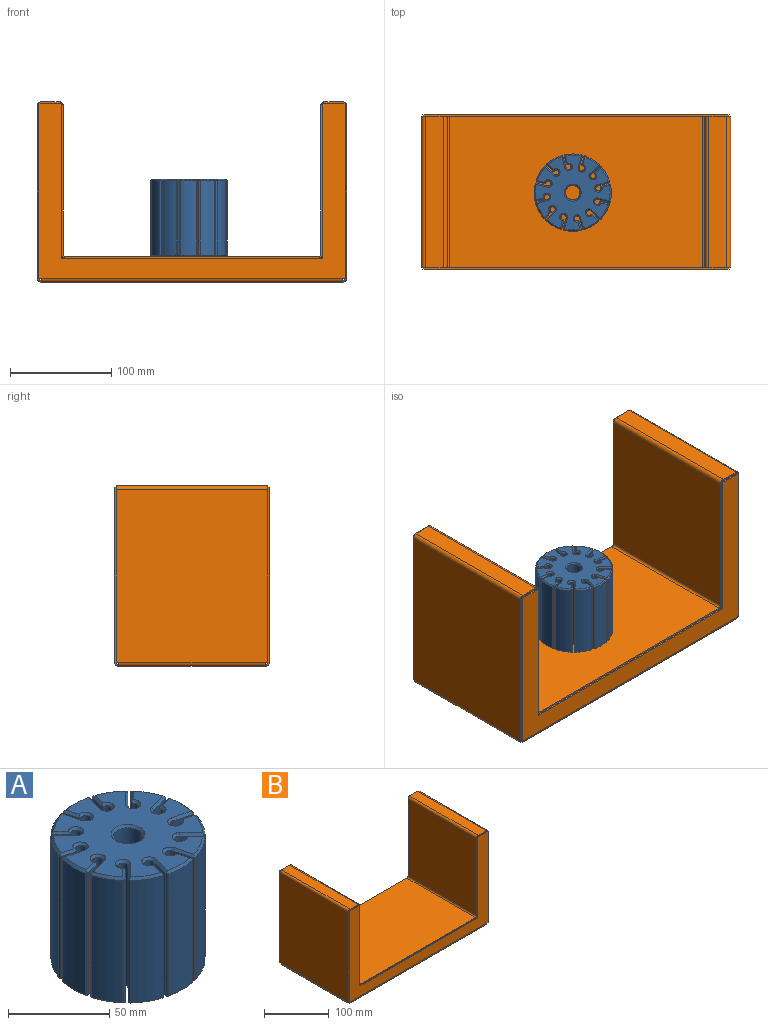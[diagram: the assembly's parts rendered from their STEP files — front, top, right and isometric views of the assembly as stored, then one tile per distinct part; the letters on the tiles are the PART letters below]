
ASSEMBLY  parts=2 mates=1
PART A: 184 faces, bbox 76.2x76.2x76.2 mm
  f0: cylinder r=2.54mm len=73.66mm, axis (0,0,-1), area 881.7mm2, adj f1,f87,f133,f172
  f1: plane 73.66x7.96mm, normal (0.71,-0.71,0), area 828.4mm2, adj f0,f85,f99,f170
  f2: cylinder r=38.1mm len=73.66mm, axis (0,0,-1), area 1179mm2, adj f83,f99,f100,f168
  f3: plane 73.66x7.12mm, normal (-0.97,0.26,0), area 543mm2, adj f81,f100,f101,f166
  f4: cylinder r=2.54mm len=73.66mm, axis (0,0,-1), area 881.7mm2, adj f5,f79,f101,f164
  f5: plane 73.66x10.87mm, normal (0.97,-0.26,0), area 828.4mm2, adj f4,f77,f102,f162
  f6: cylinder r=38.1mm len=73.66mm, axis (0,0,-1), area 1179mm2, adj f75,f102,f103,f160
  f7: plane 73.66x7.12mm, normal (-0.97,-0.26,0), area 543mm2, adj f73,f103,f104,f158
  f8: cylinder r=2.54mm len=73.66mm, axis (0,0,-1), area 881.7mm2, adj f9,f71,f104,f156
  f9: plane 73.66x10.86mm, normal (0.97,0.26,0), area 828.4mm2, adj f8,f69,f105,f154
  f10: cylinder r=38.1mm len=73.66mm, axis (0,0,-1), area 1179mm2, adj f67,f105,f106,f152
  f11: plane 73.66x5.22mm, normal (-0.71,-0.71,0), area 543mm2, adj f65,f106,f107,f150
  f12: cylinder r=2.54mm len=73.66mm, axis (0,0,-1), area 881.7mm2, adj f13,f63,f107,f148
  f13: plane 73.66x8.88mm, normal (0.71,0.71,0), area 923.6mm2, adj f12,f14,f61,f146
  f14: cylinder r=38.1mm len=73.66mm, axis (0,0,-1), area 1275.7mm2, adj f13,f59,f108,f144
  f15: plane 73.66x7.12mm, normal (-0.26,-0.97,0), area 543mm2, adj f57,f108,f109,f142
  f16: cylinder r=2.54mm len=73.66mm, axis (0,0,-1), area 881.7mm2, adj f17,f55,f109,f140
  f17: plane 73.66x10.87mm, normal (0.26,0.97,0), area 828.4mm2, adj f16,f53,f110,f138
  f18: cylinder r=38.1mm len=73.66mm, axis (0,0,-1), area 1179mm2, adj f51,f110,f111,f136
  f19: plane 73.66x7.12mm, normal (0.26,-0.97,0), area 543mm2, adj f50,f111,f112,f135
  f20: cylinder r=2.54mm len=73.66mm, axis (0,0,-1), area 881.7mm2, adj f21,f52,f112,f137
  f21: plane 73.66x10.86mm, normal (-0.26,0.97,0), area 828.4mm2, adj f20,f54,f113,f139
  f22: cylinder r=38.1mm len=73.66mm, axis (0,0,-1), area 1179mm2, adj f56,f113,f114,f141
  f23: plane 73.66x5.22mm, normal (0.71,-0.71,0), area 543mm2, adj f58,f114,f115,f143
  f24: cylinder r=2.54mm len=73.66mm, axis (0,0,-1), area 881.7mm2, adj f25,f60,f115,f145
  f25: plane 73.66x7.96mm, normal (-0.71,0.71,0), area 828.4mm2, adj f24,f62,f116,f147
  f26: cylinder r=38.1mm len=73.66mm, axis (0,0,-1), area 1179mm2, adj f64,f116,f117,f149
  f27: plane 73.66x7.12mm, normal (0.97,-0.26,0), area 543mm2, adj f66,f117,f118,f151
  f28: cylinder r=2.54mm len=73.66mm, axis (0,0,-1), area 881.7mm2, adj f29,f68,f118,f153
  f29: plane 73.66x10.87mm, normal (-0.97,0.26,0), area 828.4mm2, adj f28,f70,f119,f155
  f30: cylinder r=38.1mm len=73.66mm, axis (0,0,-1), area 1179mm2, adj f72,f119,f120,f157
  f31: plane 73.66x7.12mm, normal (0.97,0.26,0), area 543mm2, adj f74,f120,f121,f159
  f32: cylinder r=2.54mm len=73.66mm, axis (0,0,-1), area 881.7mm2, adj f33,f76,f121,f161
  f33: plane 73.66x10.86mm, normal (-0.97,-0.26,0), area 828.4mm2, adj f32,f78,f122,f163
  f34: cylinder r=38.1mm len=73.66mm, axis (0,0,-1), area 1179mm2, adj f80,f122,f123,f165
  f35: plane 73.66x5.22mm, normal (0.71,0.71,0), area 543mm2, adj f82,f123,f124,f167
  f36: cylinder r=2.54mm len=73.66mm, axis (0,0,-1), area 881.7mm2, adj f37,f84,f124,f169
  f37: plane 73.66x7.96mm, normal (-0.71,-0.71,0), area 828.4mm2, adj f36,f86,f125,f171
  f38: cylinder r=38.1mm len=73.66mm, axis (0,0,-1), area 1179mm2, adj f88,f125,f126,f173
  f39: plane 73.66x7.12mm, normal (0.26,0.97,0), area 543mm2, adj f90,f126,f127,f175
  f40: cylinder r=2.54mm len=73.66mm, axis (0,0,-1), area 881.7mm2, adj f41,f92,f127,f177
  f41: plane 73.66x10.87mm, normal (-0.26,-0.97,0), area 828.4mm2, adj f40,f94,f128,f179
  f42: cylinder r=38.1mm len=73.66mm, axis (0,0,-1), area 1179mm2, adj f96,f128,f129,f181
  f43: plane 73.66x7.12mm, normal (-0.26,0.97,0), area 543mm2, adj f97,f129,f130,f182
  f44: cylinder r=2.54mm len=73.66mm, axis (0,0,-1), area 881.7mm2, adj f45,f95,f130,f180
  f45: plane 73.66x10.86mm, normal (0.26,-0.97,0), area 828.4mm2, adj f44,f93,f131,f178
  f46: cylinder r=38.1mm len=73.66mm, axis (0,0,-1), area 1179mm2, adj f91,f131,f132,f176
  f47: plane 73.66x5.22mm, normal (-0.71,0.71,0), area 543mm2, adj f89,f132,f133,f174
  f48: plane 73.66x73.66mm, normal (0,0,-1), area 3114.7mm2, adj f50,f51,f52,f53,f54,f55,f56,f57
  f49: cylinder r=7.14mm len=73.66mm, axis (0,0,-1), area 3303.3mm2, adj f98,f183
  f50: plane 8.93x3.2mm, normal (0.18,-0.68,-0.71), area 15.1mm2, adj f19,f48,f51,f52,f111,f112
  f51: cone r=38.1mm half-angle=45deg, axis (0,0,1), area 30.1mm2, adj f18,f48,f50,f53,f110,f111
  f52: cone r=3.81mm half-angle=45deg, axis (0,0,-1), area 27.7mm2, adj f20,f48,f50,f54,f112
  f53: plane 11.85x4.18mm, normal (0.18,0.68,-0.71), area 21.1mm2, adj f17,f48,f51,f55,f110
  f54: plane 11.98x4.16mm, normal (-0.18,0.68,-0.71), area 21.1mm2, adj f21,f48,f52,f56,f113
  f55: cone r=3.81mm half-angle=45deg, axis (0,0,-1), area 27.7mm2, adj f16,f48,f53,f57,f109
  f56: cone r=38.1mm half-angle=45deg, axis (0,0,1), area 30.1mm2, adj f22,f48,f54,f58,f113,f114
  f57: plane 8.96x3.18mm, normal (-0.18,-0.68,-0.71), area 15.1mm2, adj f15,f48,f55,f59,f108,f109
  f58: plane 6.58x6.52mm, normal (0.5,-0.5,-0.71), area 15.1mm2, adj f23,f48,f56,f60,f114,f115
  f59: cone r=38.1mm half-angle=45deg, axis (0,0,1), area 30.4mm2, adj f14,f48,f57,f61,f108
  f60: cone r=3.81mm half-angle=45deg, axis (0,0,-1), area 27.7mm2, adj f24,f48,f58,f62,f115
  f61: plane 9.77x8.9mm, normal (0.5,0.5,-0.71), area 21.4mm2, adj f13,f48,f59,f63
  f62: plane 9.22x8.88mm, normal (-0.5,0.5,-0.71), area 21.1mm2, adj f25,f48,f60,f64,f116
  f63: cone r=3.81mm half-angle=45deg, axis (0,0,-1), area 27.7mm2, adj f12,f48,f61,f65,f107
  f64: cone r=38.1mm half-angle=45deg, axis (0,0,1), area 30.1mm2, adj f26,f48,f62,f66,f116,f117
  f65: plane 6.58x6.52mm, normal (-0.5,-0.5,-0.71), area 15.1mm2, adj f11,f48,f63,f67,f106,f107
  f66: plane 8.96x3.18mm, normal (0.68,-0.18,-0.71), area 15.1mm2, adj f27,f48,f64,f68,f117,f118
  f67: cone r=38.1mm half-angle=45deg, axis (0,0,1), area 30.1mm2, adj f10,f48,f65,f69,f105,f106
  f68: cone r=3.81mm half-angle=45deg, axis (0,0,-1), area 27.7mm2, adj f28,f48,f66,f70,f118
  f69: plane 11.98x4.16mm, normal (0.68,0.18,-0.71), area 21.1mm2, adj f9,f48,f67,f71,f105
  f70: plane 11.85x4.18mm, normal (-0.68,0.18,-0.71), area 21.1mm2, adj f29,f48,f68,f72,f119
  f71: cone r=3.81mm half-angle=45deg, axis (0,0,-1), area 27.7mm2, adj f8,f48,f69,f73,f104
  f72: cone r=38.1mm half-angle=45deg, axis (0,0,1), area 30.1mm2, adj f30,f48,f70,f74,f119,f120
  f73: plane 8.93x3.2mm, normal (-0.68,-0.18,-0.71), area 15.1mm2, adj f7,f48,f71,f75,f103,f104
  f74: plane 8.93x3.2mm, normal (0.68,0.18,-0.71), area 15.1mm2, adj f31,f48,f72,f76,f120,f121
  f75: cone r=38.1mm half-angle=45deg, axis (0,0,1), area 30.1mm2, adj f6,f48,f73,f77,f102,f103
  f76: cone r=3.81mm half-angle=45deg, axis (0,0,-1), area 27.7mm2, adj f32,f48,f74,f78,f121
  f77: plane 11.85x4.18mm, normal (0.68,-0.18,-0.71), area 21.1mm2, adj f5,f48,f75,f79,f102
  f78: plane 11.98x4.16mm, normal (-0.68,-0.18,-0.71), area 21.1mm2, adj f33,f48,f76,f80,f122
  f79: cone r=3.81mm half-angle=45deg, axis (0,0,-1), area 27.7mm2, adj f4,f48,f77,f81,f101
  f80: cone r=38.1mm half-angle=45deg, axis (0,0,1), area 30.1mm2, adj f34,f48,f78,f82,f122,f123
  f81: plane 8.96x3.18mm, normal (-0.68,0.18,-0.71), area 15.1mm2, adj f3,f48,f79,f83,f100,f101
  f82: plane 6.58x6.52mm, normal (0.5,0.5,-0.71), area 15.1mm2, adj f35,f48,f80,f84,f123,f124
  f83: cone r=38.1mm half-angle=45deg, axis (0,0,1), area 30.1mm2, adj f2,f48,f81,f85,f99,f100
  f84: cone r=3.81mm half-angle=45deg, axis (0,0,-1), area 27.7mm2, adj f36,f48,f82,f86,f124
  f85: plane 9.22x8.88mm, normal (0.5,-0.5,-0.71), area 21.1mm2, adj f1,f48,f83,f87,f99
  f86: plane 9.22x8.88mm, normal (-0.5,-0.5,-0.71), area 21.1mm2, adj f37,f48,f84,f88,f125
  f87: cone r=3.81mm half-angle=45deg, axis (0,0,-1), area 27.7mm2, adj f0,f48,f85,f89,f133
  f88: cone r=38.1mm half-angle=45deg, axis (0,0,1), area 30.1mm2, adj f38,f48,f86,f90,f125,f126
  f89: plane 6.58x6.52mm, normal (-0.5,0.5,-0.71), area 15.1mm2, adj f47,f48,f87,f91,f132,f133
  f90: plane 8.96x3.18mm, normal (0.18,0.68,-0.71), area 15.1mm2, adj f39,f48,f88,f92,f126,f127
  f91: cone r=38.1mm half-angle=45deg, axis (0,0,1), area 30.1mm2, adj f46,f48,f89,f93,f131,f132
  f92: cone r=3.81mm half-angle=45deg, axis (0,0,-1), area 27.7mm2, adj f40,f48,f90,f94,f127
  f93: plane 11.98x4.16mm, normal (0.18,-0.68,-0.71), area 21.1mm2, adj f45,f48,f91,f95,f131
  f94: plane 11.85x4.18mm, normal (-0.18,-0.68,-0.71), area 21.1mm2, adj f41,f48,f92,f96,f128
  f95: cone r=3.81mm half-angle=45deg, axis (0,0,-1), area 27.7mm2, adj f44,f48,f93,f97,f130
  f96: cone r=38.1mm half-angle=45deg, axis (0,0,1), area 30.1mm2, adj f42,f48,f94,f97,f128,f129
  f97: plane 8.93x3.2mm, normal (-0.18,0.68,-0.71), area 15.1mm2, adj f43,f48,f95,f96,f129,f130
  f98: cone r=7.14mm half-angle=45deg, axis (0,0,-1), area 87.7mm2, adj f48,f49
  f99: cylinder r=1.27mm len=74.42mm, axis (0,0,-1), area 150.7mm2, adj f1,f2,f83,f85,f168,f170
  f100: cylinder r=1.27mm len=74.46mm, axis (0,0,-1), area 154mm2, adj f2,f3,f81,f83,f166,f168
  f101: cylinder r=1.27mm len=74.53mm, axis (0,0,-1), area 147.5mm2, adj f3,f4,f79,f81,f164,f166
  f102: cylinder r=1.27mm len=74.42mm, axis (0,0,-1), area 150.7mm2, adj f5,f6,f75,f77,f160,f162
  f103: cylinder r=1.27mm len=74.46mm, axis (0,0,-1), area 154mm2, adj f6,f7,f73,f75,f158,f160
  f104: cylinder r=1.27mm len=74.53mm, axis (0,0,-1), area 147.5mm2, adj f7,f8,f71,f73,f156,f158
  f105: cylinder r=1.27mm len=74.42mm, axis (0,0,-1), area 150.7mm2, adj f9,f10,f67,f69,f152,f154
  f106: cylinder r=1.27mm len=74.46mm, axis (0,0,-1), area 154mm2, adj f10,f11,f65,f67,f150,f152
  f107: cylinder r=1.27mm len=74.53mm, axis (0,0,-1), area 147.5mm2, adj f11,f12,f63,f65,f148,f150
  f108: cylinder r=1.27mm len=74.46mm, axis (0,0,-1), area 154mm2, adj f14,f15,f57,f59,f142,f144
  f109: cylinder r=1.27mm len=74.53mm, axis (0,0,-1), area 147.5mm2, adj f15,f16,f55,f57,f140,f142
  f110: cylinder r=1.27mm len=74.42mm, axis (0,0,-1), area 150.7mm2, adj f17,f18,f51,f53,f136,f138
  f111: cylinder r=1.27mm len=74.46mm, axis (0,0,-1), area 154mm2, adj f18,f19,f50,f51,f135,f136
  f112: cylinder r=1.27mm len=74.53mm, axis (0,0,-1), area 147.5mm2, adj f19,f20,f50,f52,f135,f137
  f113: cylinder r=1.27mm len=74.42mm, axis (0,0,-1), area 150.7mm2, adj f21,f22,f54,f56,f139,f141
  f114: cylinder r=1.27mm len=74.46mm, axis (0,0,-1), area 154mm2, adj f22,f23,f56,f58,f141,f143
  f115: cylinder r=1.27mm len=74.53mm, axis (0,0,-1), area 147.5mm2, adj f23,f24,f58,f60,f143,f145
  f116: cylinder r=1.27mm len=74.42mm, axis (0,0,-1), area 150.7mm2, adj f25,f26,f62,f64,f147,f149
  f117: cylinder r=1.27mm len=74.46mm, axis (0,0,-1), area 154mm2, adj f26,f27,f64,f66,f149,f151
  f118: cylinder r=1.27mm len=74.53mm, axis (0,0,-1), area 147.5mm2, adj f27,f28,f66,f68,f151,f153
  f119: cylinder r=1.27mm len=74.42mm, axis (0,0,-1), area 150.7mm2, adj f29,f30,f70,f72,f155,f157
  f120: cylinder r=1.27mm len=74.46mm, axis (0,0,-1), area 154mm2, adj f30,f31,f72,f74,f157,f159
  f121: cylinder r=1.27mm len=74.53mm, axis (0,0,-1), area 147.5mm2, adj f31,f32,f74,f76,f159,f161
  f122: cylinder r=1.27mm len=74.42mm, axis (0,0,-1), area 150.7mm2, adj f33,f34,f78,f80,f163,f165
  f123: cylinder r=1.27mm len=74.46mm, axis (0,0,-1), area 154mm2, adj f34,f35,f80,f82,f165,f167
  f124: cylinder r=1.27mm len=74.53mm, axis (0,0,-1), area 147.5mm2, adj f35,f36,f82,f84,f167,f169
  f125: cylinder r=1.27mm len=74.42mm, axis (0,0,-1), area 150.7mm2, adj f37,f38,f86,f88,f171,f173
  f126: cylinder r=1.27mm len=74.46mm, axis (0,0,-1), area 154mm2, adj f38,f39,f88,f90,f173,f175
  f127: cylinder r=1.27mm len=74.53mm, axis (0,0,-1), area 147.5mm2, adj f39,f40,f90,f92,f175,f177
  f128: cylinder r=1.27mm len=74.42mm, axis (0,0,-1), area 150.7mm2, adj f41,f42,f94,f96,f179,f181
  f129: cylinder r=1.27mm len=74.46mm, axis (0,0,-1), area 154mm2, adj f42,f43,f96,f97,f181,f182
  f130: cylinder r=1.27mm len=74.53mm, axis (0,0,-1), area 147.5mm2, adj f43,f44,f95,f97,f180,f182
  f131: cylinder r=1.27mm len=74.42mm, axis (0,0,-1), area 150.7mm2, adj f45,f46,f91,f93,f176,f178
  f132: cylinder r=1.27mm len=74.46mm, axis (0,0,-1), area 154mm2, adj f46,f47,f89,f91,f174,f176
  f133: cylinder r=1.27mm len=74.53mm, axis (0,0,-1), area 147.5mm2, adj f0,f47,f87,f89,f172,f174
  f134: plane 73.66x73.66mm, normal (0,0,1), area 3114.7mm2, adj f135,f136,f137,f138,f139,f140,f141,f142
  f135: plane 8.93x3.2mm, normal (0.18,-0.68,0.71), area 15.1mm2, adj f19,f111,f112,f134,f136,f137
  f136: cone r=38.1mm half-angle=45deg, axis (0,0,-1), area 30.1mm2, adj f18,f110,f111,f134,f135,f138
  f137: cone r=3.81mm half-angle=45deg, axis (0,0,1), area 27.7mm2, adj f20,f112,f134,f135,f139
  f138: plane 11.85x4.18mm, normal (0.18,0.68,0.71), area 21.1mm2, adj f17,f110,f134,f136,f140
  f139: plane 11.98x4.16mm, normal (-0.18,0.68,0.71), area 21.1mm2, adj f21,f113,f134,f137,f141
  f140: cone r=3.81mm half-angle=45deg, axis (0,0,1), area 27.7mm2, adj f16,f109,f134,f138,f142
  f141: cone r=38.1mm half-angle=45deg, axis (0,0,-1), area 30.1mm2, adj f22,f113,f114,f134,f139,f143
  f142: plane 8.96x3.18mm, normal (-0.18,-0.68,0.71), area 15.1mm2, adj f15,f108,f109,f134,f140,f144
  f143: plane 6.58x6.52mm, normal (0.5,-0.5,0.71), area 15.1mm2, adj f23,f114,f115,f134,f141,f145
  f144: cone r=38.1mm half-angle=45deg, axis (0,0,-1), area 30.4mm2, adj f14,f108,f134,f142,f146
  f145: cone r=3.81mm half-angle=45deg, axis (0,0,1), area 27.7mm2, adj f24,f115,f134,f143,f147
  f146: plane 9.77x8.9mm, normal (0.5,0.5,0.71), area 21.4mm2, adj f13,f134,f144,f148
  f147: plane 9.22x8.88mm, normal (-0.5,0.5,0.71), area 21.1mm2, adj f25,f116,f134,f145,f149
  f148: cone r=3.81mm half-angle=45deg, axis (0,0,1), area 27.7mm2, adj f12,f107,f134,f146,f150
  f149: cone r=38.1mm half-angle=45deg, axis (0,0,-1), area 30.1mm2, adj f26,f116,f117,f134,f147,f151
  f150: plane 6.58x6.52mm, normal (-0.5,-0.5,0.71), area 15.1mm2, adj f11,f106,f107,f134,f148,f152
  f151: plane 8.96x3.18mm, normal (0.68,-0.18,0.71), area 15.1mm2, adj f27,f117,f118,f134,f149,f153
  f152: cone r=38.1mm half-angle=45deg, axis (0,0,-1), area 30.1mm2, adj f10,f105,f106,f134,f150,f154
  f153: cone r=3.81mm half-angle=45deg, axis (0,0,1), area 27.7mm2, adj f28,f118,f134,f151,f155
  f154: plane 11.98x4.16mm, normal (0.68,0.18,0.71), area 21.1mm2, adj f9,f105,f134,f152,f156
  f155: plane 11.85x4.18mm, normal (-0.68,0.18,0.71), area 21.1mm2, adj f29,f119,f134,f153,f157
  f156: cone r=3.81mm half-angle=45deg, axis (0,0,1), area 27.7mm2, adj f8,f104,f134,f154,f158
  f157: cone r=38.1mm half-angle=45deg, axis (0,0,-1), area 30.1mm2, adj f30,f119,f120,f134,f155,f159
  f158: plane 8.93x3.2mm, normal (-0.68,-0.18,0.71), area 15.1mm2, adj f7,f103,f104,f134,f156,f160
  f159: plane 8.93x3.2mm, normal (0.68,0.18,0.71), area 15.1mm2, adj f31,f120,f121,f134,f157,f161
  f160: cone r=38.1mm half-angle=45deg, axis (0,0,-1), area 30.1mm2, adj f6,f102,f103,f134,f158,f162
  f161: cone r=3.81mm half-angle=45deg, axis (0,0,1), area 27.7mm2, adj f32,f121,f134,f159,f163
  f162: plane 11.85x4.18mm, normal (0.68,-0.18,0.71), area 21.1mm2, adj f5,f102,f134,f160,f164
  f163: plane 11.98x4.16mm, normal (-0.68,-0.18,0.71), area 21.1mm2, adj f33,f122,f134,f161,f165
  f164: cone r=3.81mm half-angle=45deg, axis (0,0,1), area 27.7mm2, adj f4,f101,f134,f162,f166
  f165: cone r=38.1mm half-angle=45deg, axis (0,0,-1), area 30.1mm2, adj f34,f122,f123,f134,f163,f167
  f166: plane 8.96x3.18mm, normal (-0.68,0.18,0.71), area 15.1mm2, adj f3,f100,f101,f134,f164,f168
  f167: plane 6.58x6.52mm, normal (0.5,0.5,0.71), area 15.1mm2, adj f35,f123,f124,f134,f165,f169
  f168: cone r=38.1mm half-angle=45deg, axis (0,0,-1), area 30.1mm2, adj f2,f99,f100,f134,f166,f170
  f169: cone r=3.81mm half-angle=45deg, axis (0,0,1), area 27.7mm2, adj f36,f124,f134,f167,f171
  f170: plane 9.22x8.88mm, normal (0.5,-0.5,0.71), area 21.1mm2, adj f1,f99,f134,f168,f172
  f171: plane 9.22x8.88mm, normal (-0.5,-0.5,0.71), area 21.1mm2, adj f37,f125,f134,f169,f173
  f172: cone r=3.81mm half-angle=45deg, axis (0,0,1), area 27.7mm2, adj f0,f133,f134,f170,f174
  f173: cone r=38.1mm half-angle=45deg, axis (0,0,-1), area 30.1mm2, adj f38,f125,f126,f134,f171,f175
  f174: plane 6.58x6.52mm, normal (-0.5,0.5,0.71), area 15.1mm2, adj f47,f132,f133,f134,f172,f176
  f175: plane 8.96x3.18mm, normal (0.18,0.68,0.71), area 15.1mm2, adj f39,f126,f127,f134,f173,f177
  f176: cone r=38.1mm half-angle=45deg, axis (0,0,-1), area 30.1mm2, adj f46,f131,f132,f134,f174,f178
  f177: cone r=3.81mm half-angle=45deg, axis (0,0,1), area 27.7mm2, adj f40,f127,f134,f175,f179
  f178: plane 11.98x4.16mm, normal (0.18,-0.68,0.71), area 21.1mm2, adj f45,f131,f134,f176,f180
  f179: plane 11.85x4.18mm, normal (-0.18,-0.68,0.71), area 21.1mm2, adj f41,f128,f134,f177,f181
  f180: cone r=3.81mm half-angle=45deg, axis (0,0,1), area 27.7mm2, adj f44,f130,f134,f178,f182
  f181: cone r=38.1mm half-angle=45deg, axis (0,0,-1), area 30.1mm2, adj f42,f128,f129,f134,f179,f182
  f182: plane 8.93x3.2mm, normal (-0.18,0.68,0.71), area 15.1mm2, adj f43,f129,f130,f134,f180,f181
  f183: cone r=7.14mm half-angle=45deg, axis (0,0,1), area 87.7mm2, adj f49,f134
PART B: 96 faces, bbox 304.8x152.4x177.8 mm
  f0: plane 2.26x1.59mm, normal (0,0,-1), area 3.6mm2, adj f6,f9,f10,f28
  f1: plane 22.17x1.59mm, normal (0,0,1), area 35.2mm2, adj f2,f8,f9,f10
  f2: plane 152.4x1.59mm, normal (1,0,0), area 241.9mm2, adj f1,f3,f9,f10
  f3: plane 257.23x1.59mm, normal (0,0,1), area 408.3mm2, adj f2,f4,f9,f10
  f4: plane 152.4x1.59mm, normal (-1,0,0), area 241.9mm2, adj f3,f5,f9,f10
  f5: plane 22.17x1.59mm, normal (0,0,1), area 35.2mm2, adj f4,f6,f9,f10
  f6: plane 172.31x1.59mm, normal (1,0,0), area 273.5mm2, adj f0,f5,f9,f10
  f7: plane 2.26x1.59mm, normal (0,0,-1), area 3.6mm2, adj f8,f9,f10,f29
  f8: plane 172.31x1.59mm, normal (-1,0,0), area 273.5mm2, adj f1,f7,f9,f10
  f9: plane 301.57x172.31mm, normal (0,1,0), area 12764.1mm2, adj f0,f1,f2,f3,f4,f5,f6,f7
  f10: plane 301.57x172.31mm, normal (0,-1,0), area 12764.1mm2, adj f0,f1,f2,f3,f4,f5,f6,f7
  f11: plane 2.26x1.59mm, normal (0,0,-1), area 3.6mm2, adj f17,f20,f21,f23
  f12: plane 22.17x1.59mm, normal (0,0,1), area 35.2mm2, adj f13,f19,f20,f21
  f13: plane 152.4x1.59mm, normal (-1,0,0), area 241.9mm2, adj f12,f14,f20,f21
  f14: plane 257.23x1.59mm, normal (0,0,1), area 408.3mm2, adj f13,f15,f20,f21
  f15: plane 152.4x1.59mm, normal (1,0,0), area 241.9mm2, adj f14,f16,f20,f21
  f16: plane 22.17x1.59mm, normal (0,0,1), area 35.2mm2, adj f15,f17,f20,f21
  f17: plane 172.31x1.59mm, normal (-1,0,0), area 273.5mm2, adj f11,f16,f20,f21
  f18: plane 2.26x1.59mm, normal (0,0,-1), area 3.6mm2, adj f19,f20,f21,f22
  f19: plane 172.31x1.59mm, normal (1,0,0), area 273.5mm2, adj f12,f18,f20,f21
  f20: plane 301.57x172.31mm, normal (0,-1,0), area 12764.1mm2, adj f11,f12,f13,f14,f15,f16,f17,f18
  f21: plane 301.57x172.31mm, normal (0,1,0), area 12764.1mm2, adj f11,f12,f13,f14,f15,f16,f17,f18
  f22: plane 3.87x3.87mm, normal (1,0,0), area 7.7mm2, adj f18,f24,f25,f32
  f23: plane 3.87x3.87mm, normal (-1,0,0), area 7.7mm2, adj f11,f24,f25,f42
  f24: cylinder r=3.87mm len=297.05mm, axis (1,0,0), area 1807.4mm2, adj f20,f22,f23,f26
  f25: cylinder r=2.29mm len=297.05mm, axis (1,0,0), area 1066.7mm2, adj f21,f22,f23,f27
  f26: plane 297.05x144.65mm, normal (0,0,-1), area 42969.6mm2, adj f24,f30,f34,f44
  f27: plane 297.05x144.65mm, normal (0,0,1), area 42969.6mm2, adj f25,f31,f35,f45
  f28: plane 3.87x3.87mm, normal (1,0,0), area 7.7mm2, adj f0,f30,f31,f33
  f29: plane 3.87x3.87mm, normal (-1,0,0), area 7.7mm2, adj f7,f30,f31,f43
  f30: cylinder r=3.87mm len=297.05mm, axis (1,0,0), area 1807.4mm2, adj f9,f26,f28,f29
  f31: cylinder r=2.29mm len=297.05mm, axis (1,0,0), area 1066.7mm2, adj f10,f27,f28,f29
  f32: plane 3.87x3.87mm, normal (0,-1,0), area 7.7mm2, adj f22,f34,f35,f36
  f33: plane 3.87x3.87mm, normal (0,1,0), area 7.7mm2, adj f28,f34,f35,f38
  f34: cylinder r=3.87mm len=144.65mm, axis (0,-1,0), area 880.1mm2, adj f26,f32,f33,f40
  f35: cylinder r=2.29mm len=144.65mm, axis (0,-1,0), area 519.4mm2, adj f27,f32,f33,f41
  f36: plane 2.26x1.59mm, normal (0,0,-1), area 3.6mm2, adj f32,f37,f40,f41
  f37: plane 170.05x1.59mm, normal (0,-1,0), area 270mm2, adj f36,f40,f41,f46
  f38: plane 2.26x1.59mm, normal (0,0,-1), area 3.6mm2, adj f33,f39,f40,f41
  f39: plane 170.05x1.59mm, normal (0,1,0), area 270mm2, adj f38,f40,f41,f47
  f40: plane 170.05x149.17mm, normal (1,0,0), area 25367.5mm2, adj f34,f36,f37,f38,f39,f48
  f41: plane 170.05x149.17mm, normal (-1,0,0), area 25367.5mm2, adj f35,f36,f37,f38,f39,f49
  f42: plane 3.87x3.87mm, normal (0,-1,0), area 7.7mm2, adj f23,f44,f45,f52
  f43: plane 3.87x3.87mm, normal (0,1,0), area 7.7mm2, adj f29,f44,f45,f50
  f44: cylinder r=3.87mm len=144.65mm, axis (0,-1,0), area 880.1mm2, adj f26,f42,f43,f54
  f45: cylinder r=2.29mm len=144.65mm, axis (0,-1,0), area 519.4mm2, adj f27,f42,f43,f55
  f46: plane 3.87x3.87mm, normal (0,-1,0), area 7.7mm2, adj f37,f48,f49,f56
  f47: plane 3.87x3.87mm, normal (0,1,0), area 7.7mm2, adj f39,f48,f49,f57
  f48: cylinder r=3.87mm len=149.17mm, axis (0,-1,0), area 907.6mm2, adj f40,f46,f47,f58
  f49: cylinder r=2.29mm len=149.17mm, axis (0,-1,0), area 535.7mm2, adj f41,f46,f47,f59
  f50: plane 2.26x1.59mm, normal (0,0,-1), area 3.6mm2, adj f43,f51,f54,f55
  f51: plane 170.05x1.59mm, normal (0,1,0), area 270mm2, adj f50,f54,f55,f61
  f52: plane 2.26x1.59mm, normal (0,0,-1), area 3.6mm2, adj f42,f53,f54,f55
  f53: plane 170.05x1.59mm, normal (0,-1,0), area 270mm2, adj f52,f54,f55,f60
  f54: plane 170.05x149.17mm, normal (-1,0,0), area 25367.5mm2, adj f44,f50,f51,f52,f53,f62
  f55: plane 170.05x149.17mm, normal (1,0,0), area 25367.5mm2, adj f45,f50,f51,f52,f53,f63
  f56: plane 17.65x1.59mm, normal (0,-1,0), area 28mm2, adj f46,f58,f59,f64
  f57: plane 17.65x1.59mm, normal (0,1,0), area 28mm2, adj f47,f58,f59,f65
  f58: plane 149.17x17.65mm, normal (0,0,1), area 2633.4mm2, adj f48,f56,f57,f66
  f59: plane 149.17x17.65mm, normal (0,0,-1), area 2633.4mm2, adj f49,f56,f57,f67
  f60: plane 3.87x3.87mm, normal (0,-1,0), area 7.7mm2, adj f53,f62,f63,f68
  f61: plane 3.87x3.87mm, normal (0,1,0), area 7.7mm2, adj f51,f62,f63,f69
  f62: cylinder r=3.87mm len=149.17mm, axis (0,-1,0), area 907.6mm2, adj f54,f60,f61,f70
  f63: cylinder r=2.29mm len=149.17mm, axis (0,-1,0), area 535.7mm2, adj f55,f60,f61,f71
  f64: plane 3.87x3.87mm, normal (0,-1,0), area 7.7mm2, adj f56,f66,f67,f77
  f65: plane 3.87x3.87mm, normal (0,1,0), area 7.7mm2, adj f57,f66,f67,f76
  f66: cylinder r=3.87mm len=149.17mm, axis (0,-1,0), area 907.6mm2, adj f58,f64,f65,f78
  f67: cylinder r=2.29mm len=149.17mm, axis (0,-1,0), area 535.7mm2, adj f59,f64,f65,f79
  f68: plane 17.65x1.59mm, normal (0,-1,0), area 28mm2, adj f60,f70,f71,f72
  f69: plane 17.65x1.59mm, normal (0,1,0), area 28mm2, adj f61,f70,f71,f73
  f70: plane 149.17x17.65mm, normal (0,0,1), area 2633.4mm2, adj f62,f68,f69,f74
  f71: plane 149.17x17.65mm, normal (0,0,-1), area 2633.4mm2, adj f63,f68,f69,f75
  f72: plane 3.87x3.87mm, normal (0,-1,0), area 7.7mm2, adj f68,f74,f75,f92
  f73: plane 3.87x3.87mm, normal (0,1,0), area 7.7mm2, adj f69,f74,f75,f93
  f74: cylinder r=3.87mm len=149.17mm, axis (0,-1,0), area 907.6mm2, adj f70,f72,f73,f94
  f75: cylinder r=2.29mm len=149.17mm, axis (0,-1,0), area 535.7mm2, adj f71,f72,f73,f95
  f76: plane 146.24x1.59mm, normal (0,1,0), area 232.2mm2, adj f65,f78,f79,f81
  f77: plane 146.24x1.59mm, normal (0,-1,0), area 232.2mm2, adj f64,f78,f79,f80
  f78: plane 149.17x146.24mm, normal (-1,0,0), area 21815.3mm2, adj f66,f76,f77,f83
  f79: plane 149.17x146.24mm, normal (1,0,0), area 21815.3mm2, adj f67,f76,f77,f82
  f80: plane 3.87x3.87mm, normal (0,-1,0), area 7.7mm2, adj f77,f82,f83,f84
  f81: plane 3.87x3.87mm, normal (0,1,0), area 7.7mm2, adj f76,f82,f83,f85
  f82: cylinder r=3.87mm len=149.17mm, axis (0,-1,0), area 907.6mm2, adj f79,f80,f81,f87
  f83: cylinder r=2.29mm len=149.17mm, axis (0,-1,0), area 535.7mm2, adj f78,f80,f81,f86
  f84: plane 249.43x1.59mm, normal (0,-1,0), area 396mm2, adj f80,f86,f87,f88
  f85: plane 249.43x1.59mm, normal (0,1,0), area 396mm2, adj f81,f86,f87,f89
  f86: plane 249.43x149.17mm, normal (0,0,1), area 37208.2mm2, adj f83,f84,f85,f91
  f87: plane 249.43x149.17mm, normal (0,0,-1), area 37208.2mm2, adj f82,f84,f85,f90
  f88: plane 3.87x3.87mm, normal (0,-1,0), area 7.7mm2, adj f84,f90,f91,f92
  f89: plane 3.87x3.87mm, normal (0,1,0), area 7.7mm2, adj f85,f90,f91,f93
  f90: cylinder r=3.87mm len=149.17mm, axis (0,-1,0), area 907.6mm2, adj f87,f88,f89,f95
  f91: cylinder r=2.29mm len=149.17mm, axis (0,-1,0), area 535.7mm2, adj f86,f88,f89,f94
  f92: plane 146.24x1.59mm, normal (0,-1,0), area 232.2mm2, adj f72,f88,f94,f95
  f93: plane 146.24x1.59mm, normal (0,1,0), area 232.2mm2, adj f73,f89,f94,f95
  f94: plane 149.17x146.24mm, normal (1,0,0), area 21815.3mm2, adj f74,f91,f92,f93
  f95: plane 149.17x146.24mm, normal (-1,0,0), area 21815.3mm2, adj f75,f90,f92,f93
PLACE A t=(-18.35,7.33,-38.48)mm
PLACE B t=(-15.11,7.95,-63.88)mm
MATE planar A.f48 <-> B.f86  axis (0,0,-1) through (0.64,-9.83,-38.48)mm
